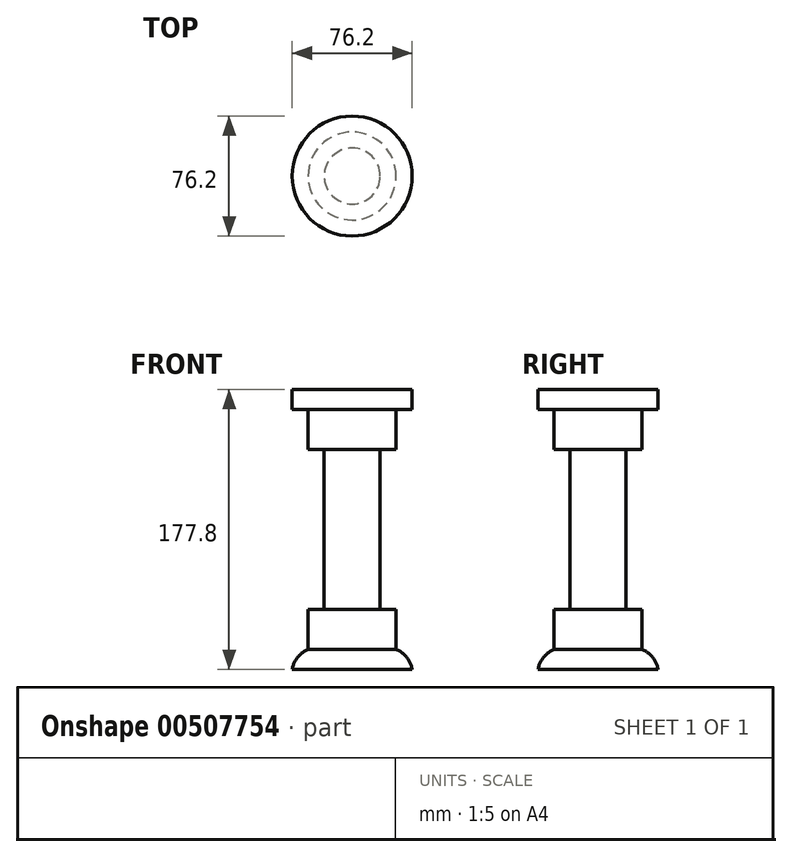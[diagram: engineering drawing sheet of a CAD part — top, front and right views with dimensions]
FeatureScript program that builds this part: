
annotation { "Feature Type Name" : "Feature", "Feature Type Description" : "" }
export const myFeature = defineFeature(function(context is Context, id is Id, definition is map)
    precondition{}
    {
        {
            var Q0;
            Q0=qCreatedBy(makeId("Front.planeOp"),FACE);
            var sketch = newSketch(context, id + "F0", { "sketchPlane" : qUnion([Q0])});
            skLineSegment(sketch, "E0", {"start": v(0, 0) * mm, "end": v(38.1, 0) * mm});
            skArc(sketch, "E1", {"start": v(38.1, 0) * mm, "mid": v(34.7, 7.69) * mm, "end": v(27.94, 12.7) * mm});
            skLineSegment(sketch, "E2", {"start": v(17.78, 38.1) * mm, "end": v(17.78, 38.1) * mm});
            skLineSegment(sketch, "E3", {"start": v(17.78, 38.1) * mm, "end": v(17.78, 139.7) * mm});
            skLineSegment(sketch, "E4", {"start": v(17.78, 139.7) * mm, "end": v(27.94, 139.7) * mm});
            skLineSegment(sketch, "E5", {"start": v(27.94, 139.7) * mm, "end": v(27.94, 165.1) * mm});
            skLineSegment(sketch, "E6", {"start": v(27.94, 165.1) * mm, "end": v(38.1, 165.1) * mm});
            skLineSegment(sketch, "E7", {"start": v(38.1, 165.1) * mm, "end": v(38.1, 177.8) * mm});
            skLineSegment(sketch, "E8", {"start": v(38.1, 177.8) * mm, "end": v(0, 177.8) * mm});
            skLineSegment(sketch, "E9", {"start": v(0, 177.8) * mm, "end": v(0, 0) * mm});
            skLineSegment(sketch, "E10", {"start": v(17.78, 38.1) * mm, "end": v(27.94, 38.1) * mm});
            skLineSegment(sketch, "E11", {"start": v(27.94, 38.1) * mm, "end": v(27.94, 12.7) * mm});
            skSolve(sketch);
        }
        {
            var Q0;
            Q0=makeQuery(id+"F0.imprint","IMPRINT",FACE,{"disambiguationData":[TD([[makeQuery(id+"F0.imprint","IMPRINT",EDGE,{"derivedFrom":sQuery(id+"F0.wireOp",EDGE,"E0")}),1.0]])]});
            var Q1;
            Q1=sQuery(id+"F0.wireOp",EDGE,"E9");
            revolve(context, id + "F1", {"entities" : qUnion([Q0]), "axis" : qUnion([Q1]), "revolveType" : RevolveType.FULL});
        }
    });
